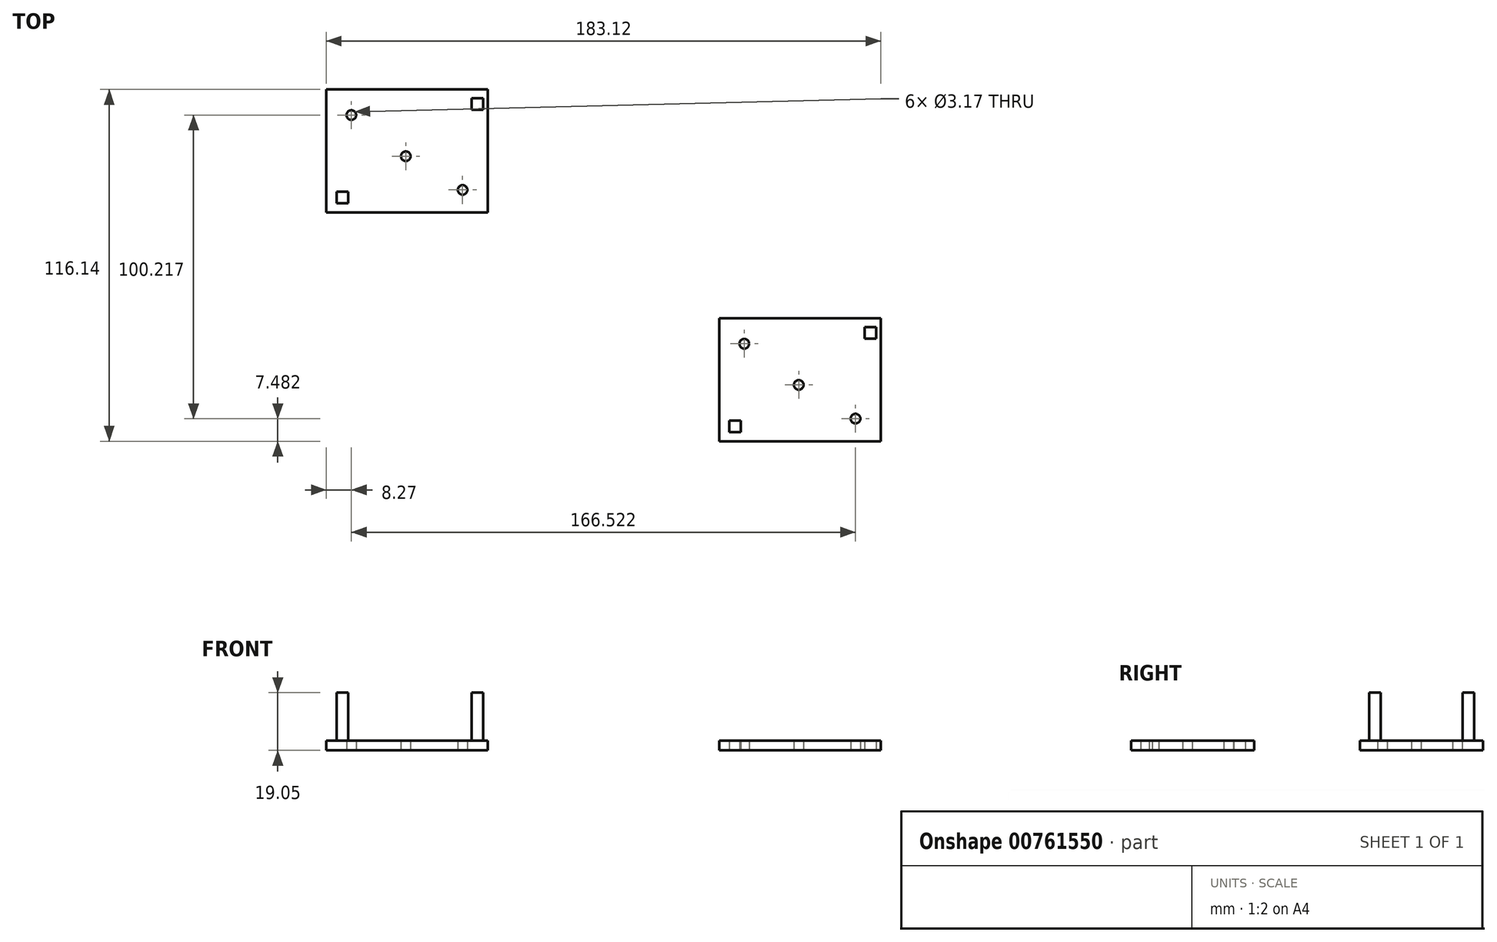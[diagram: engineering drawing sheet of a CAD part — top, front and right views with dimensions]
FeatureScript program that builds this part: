
annotation { "Feature Type Name" : "Feature", "Feature Type Description" : "" }
export const myFeature = defineFeature(function(context is Context, id is Id, definition is map)
    precondition{}
    {
        {
            var Q0;
            Q0=qCreatedBy(makeId("Top.planeOp"),FACE);
            var sketch = newSketch(context, id + "F0", { "sketchPlane" : qUnion([Q0])});
            skLineSegment(sketch, "E0.bottom", {"start": v(27.13, -9.57) * mm, "end": v(80.47, -9.57) * mm});
            skLineSegment(sketch, "E0.top", {"start": v(27.13, -50.21) * mm, "end": v(80.47, -50.21) * mm});
            skLineSegment(sketch, "E0.left", {"start": v(27.13, -9.57) * mm, "end": v(27.13, -50.21) * mm});
            skLineSegment(sketch, "E0.right", {"start": v(80.47, -9.57) * mm, "end": v(80.47, -50.21) * mm});
            skCircle(sketch, "E1", {"center": v(35.4, -18.01) * mm, "radius": 6.35 * mm});
            skCircle(sketch, "E2", {"center": v(53.38, -31.6) * mm, "radius": 15.88 * mm});
            skCircle(sketch, "E3", {"center": v(72.14, -42.73) * mm, "radius": 5.72 * mm});
            skCircle(sketch, "E4", {"center": v(35.4, -18.01) * mm, "radius": 1.59 * mm});
            skCircle(sketch, "E5", {"center": v(53.38, -31.6) * mm, "radius": 1.59 * mm});
            skCircle(sketch, "E6", {"center": v(72.14, -42.73) * mm, "radius": 1.59 * mm});
            skLineSegment(sketch, "E7.bottom", {"start": v(75.16, -16.3) * mm, "end": v(78.97, -16.3) * mm});
            skLineSegment(sketch, "E7.top", {"start": v(75.16, -12.49) * mm, "end": v(78.97, -12.49) * mm});
            skLineSegment(sketch, "E7.left", {"start": v(75.16, -16.3) * mm, "end": v(75.16, -12.49) * mm});
            skLineSegment(sketch, "E7.right", {"start": v(78.97, -16.3) * mm, "end": v(78.97, -12.49) * mm});
            skLineSegment(sketch, "E8.bottom", {"start": v(30.49, -47.13) * mm, "end": v(34.3, -47.13) * mm});
            skLineSegment(sketch, "E8.top", {"start": v(30.49, -43.32) * mm, "end": v(34.3, -43.32) * mm});
            skLineSegment(sketch, "E8.left", {"start": v(30.49, -47.13) * mm, "end": v(30.49, -43.32) * mm});
            skLineSegment(sketch, "E8.right", {"start": v(34.3, -47.13) * mm, "end": v(34.3, -43.32) * mm});
            skLineSegment(sketch, "E9.bottom", {"start": v(-102.65, 65.93) * mm, "end": v(-49.3, 65.93) * mm});
            skLineSegment(sketch, "E9.top", {"start": v(-102.65, 25.3) * mm, "end": v(-49.3, 25.3) * mm});
            skLineSegment(sketch, "E9.left", {"start": v(-102.65, 65.93) * mm, "end": v(-102.65, 25.3) * mm});
            skLineSegment(sketch, "E9.right", {"start": v(-49.3, 65.93) * mm, "end": v(-49.3, 25.3) * mm});
            skCircle(sketch, "E10", {"center": v(-94.38, 57.49) * mm, "radius": 6.35 * mm});
            skCircle(sketch, "E11", {"center": v(-76.4, 43.9) * mm, "radius": 15.88 * mm});
            skCircle(sketch, "E12", {"center": v(-57.63, 32.78) * mm, "radius": 5.72 * mm});
            skCircle(sketch, "E13", {"center": v(-94.38, 57.49) * mm, "radius": 1.59 * mm});
            skCircle(sketch, "E14", {"center": v(-76.4, 43.9) * mm, "radius": 1.59 * mm});
            skCircle(sketch, "E15", {"center": v(-57.63, 32.78) * mm, "radius": 1.59 * mm});
            skLineSegment(sketch, "E16.bottom", {"start": v(-54.61, 59.2) * mm, "end": v(-50.8, 59.2) * mm});
            skLineSegment(sketch, "E16.top", {"start": v(-54.61, 63.01) * mm, "end": v(-50.8, 63.01) * mm});
            skLineSegment(sketch, "E16.left", {"start": v(-54.61, 59.2) * mm, "end": v(-54.61, 63.01) * mm});
            skLineSegment(sketch, "E16.right", {"start": v(-50.8, 59.2) * mm, "end": v(-50.8, 63.01) * mm});
            skLineSegment(sketch, "E17.bottom", {"start": v(-99.29, 28.38) * mm, "end": v(-95.48, 28.38) * mm});
            skLineSegment(sketch, "E17.top", {"start": v(-99.29, 32.19) * mm, "end": v(-95.48, 32.19) * mm});
            skLineSegment(sketch, "E17.left", {"start": v(-99.29, 28.38) * mm, "end": v(-99.29, 32.19) * mm});
            skLineSegment(sketch, "E17.right", {"start": v(-95.48, 28.38) * mm, "end": v(-95.48, 32.19) * mm});
            skSolve(sketch);
        }
        {
            var Q0;
            Q0=makeQuery(id+"F0.imprint","IMPRINT",FACE,{"disambiguationData":[TD([[makeQuery(id+"F0.imprint","IMPRINT",EDGE,{"derivedFrom":sQuery(id+"F0.wireOp",EDGE,"E0.bottom")}),-1.0]])]});
            var Q1;
            Q1=makeQuery(id+"F0.imprint","IMPRINT",FACE,{"disambiguationData":[TD([[makeQuery(id+"F0.imprint","IMPRINT",EDGE,{"derivedFrom":sQuery(id+"F0.wireOp",EDGE,"E2")}),1.0]])]});
            var Q2;
            Q2=makeQuery(id+"F0.imprint","IMPRINT",FACE,{"disambiguationData":[TD([[makeQuery(id+"F0.imprint","IMPRINT",EDGE,{"derivedFrom":sQuery(id+"F0.wireOp",EDGE,"E3")}),1.0]])]});
            var Q3;
            Q3=makeQuery(id+"F0.imprint","IMPRINT",FACE,{"disambiguationData":[TD([[makeQuery(id+"F0.imprint","IMPRINT",EDGE,{"derivedFrom":sQuery(id+"F0.wireOp",EDGE,"E1")}),1.0]])]});
            extrude(context, id + "F1", {"entities" : qUnion([Q0, Q1, Q2, Q3]), "depth" : 3.17 * mm, "offsetDistance" : 25.4 * mm});
        }
        {
            var Q0;
            Q0=makeQuery(id+"F0.imprint","IMPRINT",FACE,{"disambiguationData":[TD([[makeQuery(id+"F0.imprint","IMPRINT",EDGE,{"derivedFrom":sQuery(id+"F0.wireOp",EDGE,"E9.bottom")}),-1.0]])]});
            var Q1;
            Q1=makeQuery(id+"F0.imprint","IMPRINT",FACE,{"disambiguationData":[TD([[makeQuery(id+"F0.imprint","IMPRINT",EDGE,{"derivedFrom":sQuery(id+"F0.wireOp",EDGE,"E12")}),1.0]])]});
            var Q2;
            Q2=makeQuery(id+"F0.imprint","IMPRINT",FACE,{"disambiguationData":[TD([[makeQuery(id+"F0.imprint","IMPRINT",EDGE,{"derivedFrom":sQuery(id+"F0.wireOp",EDGE,"E11")}),1.0]])]});
            var Q3;
            Q3=makeQuery(id+"F0.imprint","IMPRINT",FACE,{"disambiguationData":[TD([[makeQuery(id+"F0.imprint","IMPRINT",EDGE,{"derivedFrom":sQuery(id+"F0.wireOp",EDGE,"E10")}),1.0]])]});
            extrude(context, id + "F2", {"entities" : qUnion([Q0, Q1, Q2, Q3]), "depth" : 3.17 * mm, "offsetDistance" : 25.4 * mm});
        }
        {
            var Q0;
            Q0=makeQuery(id+"F0.imprint","IMPRINT",FACE,{"disambiguationData":[TD([[makeQuery(id+"F0.imprint","IMPRINT",EDGE,{"derivedFrom":sQuery(id+"F0.wireOp",EDGE,"E17.bottom")}),1.0]])]});
            var Q1;
            Q1=makeQuery(id+"F0.imprint","IMPRINT",FACE,{"disambiguationData":[TD([[makeQuery(id+"F0.imprint","IMPRINT",EDGE,{"derivedFrom":sQuery(id+"F0.wireOp",EDGE,"E16.bottom")}),1.0]])]});
            extrude(context, id + "F3", {"entities" : qUnion([Q0, Q1]), "operationType" : NewBodyOperationType.ADD, "depth" : 19.05 * mm, "offsetDistance" : 25.4 * mm});
        }
    });
